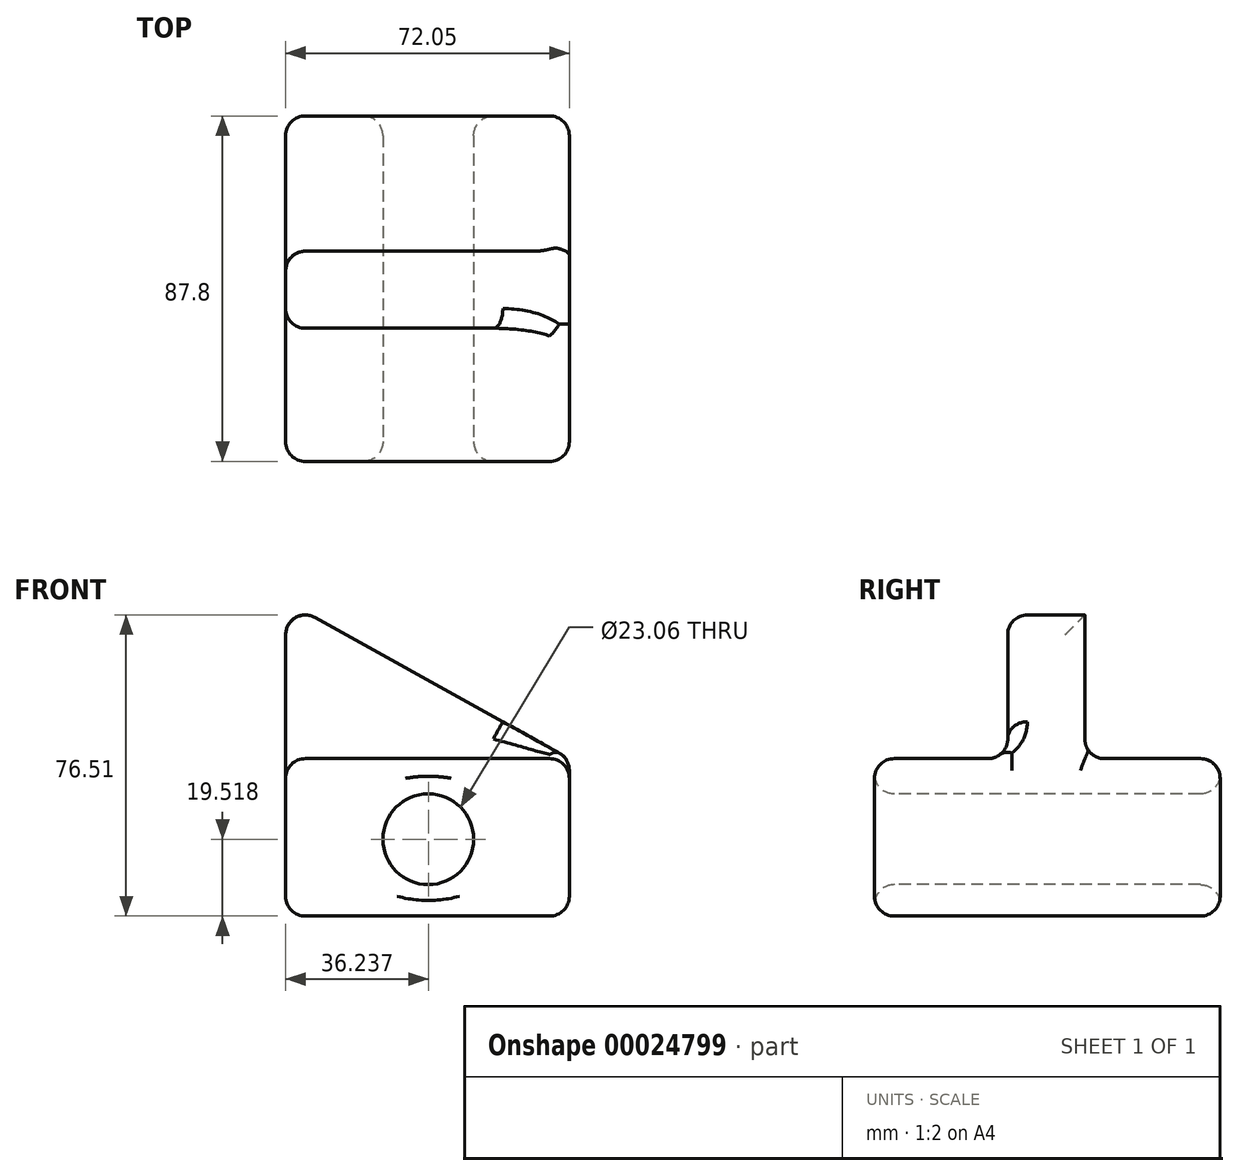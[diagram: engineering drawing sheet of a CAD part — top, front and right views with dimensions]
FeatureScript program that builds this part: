
annotation { "Feature Type Name" : "Feature", "Feature Type Description" : "" }
export const myFeature = defineFeature(function(context is Context, id is Id, definition is map)
    precondition{}
    {
        {
            var Q0;
            Q0=qCreatedBy(makeId("Top.planeOp"),FACE);
            var sketch = newSketch(context, id + "F0", { "sketchPlane" : qUnion([Q0])});
            skLineSegment(sketch, "E0.bottom", {"start": v(-59.89, -44.54) * mm, "end": v(12.16, -44.54) * mm});
            skLineSegment(sketch, "E0.top", {"start": v(-59.89, 43.26) * mm, "end": v(12.16, 43.26) * mm});
            skLineSegment(sketch, "E0.left", {"start": v(-59.89, -44.54) * mm, "end": v(-59.89, 43.26) * mm});
            skLineSegment(sketch, "E0.right", {"start": v(12.16, -44.54) * mm, "end": v(12.16, 43.26) * mm});
            skSolve(sketch);
        }
        {
            var Q0;
            Q0=makeQuery(id+"F0.imprint","IMPRINT",FACE,{"disambiguationData":[TD([[makeQuery(id+"F0.imprint","IMPRINT",EDGE,{"derivedFrom":sQuery(id+"F0.wireOp",EDGE,"E0.bottom")}),1.0]])]});
            extrude(context, id + "F1", {"entities" : qUnion([Q0]), "depth" : 40 * mm});
        }
        {
            var Q0;
            Q0=makeQuery(id+"F1.opExtrude","SWEPT_FACE",FACE,{"disambiguationData":[OSD([sQuery(id+"F0.wireOp",EDGE,"E0.bottom")])]});
            var sketch = newSketch(context, id + "F2", { "sketchPlane" : qUnion([Q0])});
            skCircle(sketch, "E1", {"center": v(-23.65, 19.52) * mm, "radius": 11.53 * mm});
            skSolve(sketch);
        }
        {
            var Q0;
            Q0=makeQuery(id+"F2.imprint","IMPRINT",FACE,{"disambiguationData":[TD([[makeQuery(id+"F2.imprint","IMPRINT",EDGE,{"derivedFrom":sQuery(id+"F2.wireOp",EDGE,"E1")}),1.0]])]});
            extrude(context, id + "F3", {"entities" : qUnion([Q0]), "operationType" : NewBodyOperationType.REMOVE, "endBound" : BoundingType.THROUGH_ALL, "oppositeDirection" : true, "depth" : 25 * mm});
        }
        {
            var Q0;
            Q0=makeQuery(id+"F1.opExtrude","CAP_FACE",FACE,{"disambiguationData":[OSD([sQuery(id+"F0.wireOp",EDGE,"E0.bottom"),sQuery(id+"F0.wireOp",EDGE,"E0.top"),sQuery(id+"F0.wireOp",EDGE,"E0.left"),sQuery(id+"F0.wireOp",EDGE,"E0.right")])],"isStart":false});
            var sketch = newSketch(context, id + "F4", { "sketchPlane" : qUnion([Q0])});
            skLineSegment(sketch, "E2.bottom", {"start": v(-59.89, -10.7) * mm, "end": v(12.16, -10.7) * mm});
            skLineSegment(sketch, "E2.top", {"start": v(-59.89, 8.88) * mm, "end": v(12.16, 8.88) * mm});
            skLineSegment(sketch, "E2.left", {"start": v(-59.89, -10.7) * mm, "end": v(-59.89, 8.88) * mm});
            skLineSegment(sketch, "E2.right", {"start": v(12.16, -10.7) * mm, "end": v(12.16, 8.88) * mm});
            skSolve(sketch);
        }
        {
            var Q0;
            Q0=makeQuery(id+"F4.imprint","IMPRINT",FACE,{"disambiguationData":[TD([[makeQuery(id+"F4.imprint","IMPRINT",EDGE,{"derivedFrom":sQuery(id+"F4.wireOp",EDGE,"E2.bottom")}),1.0]])]});
            extrude(context, id + "F5", {"entities" : qUnion([Q0]), "operationType" : NewBodyOperationType.ADD, "depth" : 40 * mm});
        }
        {
            var Q0;
            Q0=makeQuery(id+"F5.opExtrude","SWEPT_FACE",FACE,{"disambiguationData":[OSD([sQuery(id+"F4.wireOp",EDGE,"E2.bottom")])]});
            var sketch = newSketch(context, id + "F6", { "sketchPlane" : qUnion([Q0])});
            skLineSegment(sketch, "E3", {"start": v(12.16, 40) * mm, "end": v(-59.89, 80) * mm});
            skSolve(sketch);
        }
        {
            var Q0;
            Q0=makeQuery(id+"F6.imprint","IMPRINT",FACE,{"disambiguationData":[TD([[makeQuery(id+"F6.imprint","IMPRINT",EDGE,{"derivedFrom":sQuery(id+"F6.wireOp",EDGE,"E3")}),-1.0]])]});
            extrude(context, id + "F7", {"entities" : qUnion([Q0]), "operationType" : NewBodyOperationType.REMOVE, "endBound" : BoundingType.THROUGH_ALL, "oppositeDirection" : true, "depth" : 25 * mm});
        }
        {
            var Q0;
            Q0=makeQuery(id+"F5.opExtrude","SWEPT_FACE",FACE,{"disambiguationData":[OSD([sQuery(id+"F4.wireOp",EDGE,"E2.bottom")])]});
            var Q1;
            {var subQ0=sQuery(id+"F0.wireOp",EDGE,"E0.bottom");var subQ1=sQuery(id+"F0.wireOp",EDGE,"E0.left");var subQ2=sQuery(id+"F0.wireOp",EDGE,"E0.right");Q1=makeQuery(id+"F5.boolean.opBoolean","SPLIT",FACE,{"disambiguationData":[TD([makeQuery(id+"F1.opExtrude","SWEPT_FACE",FACE,{"disambiguationData":[OSD([subQ0])]})])],"derivedFrom":makeQuery(id+"F1.opExtrude","CAP_FACE",FACE,{"disambiguationData":[OSD([subQ0,sQuery(id+"F0.wireOp",EDGE,"E0.top"),subQ1,subQ2])],"isStart":false})});}
            var Q2;
            {var subQ0=sQuery(id+"F0.wireOp",EDGE,"E0.top");var subQ1=sQuery(id+"F0.wireOp",EDGE,"E0.left");var subQ2=sQuery(id+"F0.wireOp",EDGE,"E0.right");Q2=makeQuery(id+"F5.boolean.opBoolean","SPLIT",FACE,{"disambiguationData":[TD([makeQuery(id+"F1.opExtrude","SWEPT_FACE",FACE,{"disambiguationData":[OSD([subQ0])]})])],"derivedFrom":makeQuery(id+"F1.opExtrude","CAP_FACE",FACE,{"disambiguationData":[OSD([sQuery(id+"F0.wireOp",EDGE,"E0.bottom"),subQ0,subQ1,subQ2])],"isStart":false})});}
            var Q3;
            Q3=makeQuery(id+"F5.boolean.opBoolean","MERGE",FACE,{"derivedFrom":[makeQuery(id+"F1.opExtrude","SWEPT_FACE",FACE,{"disambiguationData":[OSD([sQuery(id+"F0.wireOp",EDGE,"E0.right")])]}),makeQuery(id+"F5.opExtrude","SWEPT_FACE",FACE,{"disambiguationData":[OSD([sQuery(id+"F4.wireOp",EDGE,"E2.right")])]})]});
            var Q4;
            Q4=makeQuery(id+"F1.opExtrude","SWEPT_FACE",FACE,{"disambiguationData":[OSD([sQuery(id+"F0.wireOp",EDGE,"E0.bottom")])]});
            var Q5;
            Q5=makeQuery(id+"F3.boolean.opBoolean","COPY",FACE,{"derivedFrom":makeQuery(id+"F3.opExtrude","SWEPT_FACE",FACE,{"disambiguationData":[OSD([sQuery(id+"F2.wireOp",EDGE,"E1")])]})});
            var Q6;
            Q6=makeQuery(id+"F5.boolean.opBoolean","MERGE",FACE,{"derivedFrom":[makeQuery(id+"F1.opExtrude","SWEPT_FACE",FACE,{"disambiguationData":[OSD([sQuery(id+"F0.wireOp",EDGE,"E0.left")])]}),makeQuery(id+"F5.opExtrude","SWEPT_FACE",FACE,{"disambiguationData":[OSD([sQuery(id+"F4.wireOp",EDGE,"E2.left")])]})]});
            var Q7;
            Q7=makeQuery(id+"F1.opExtrude","CAP_FACE",FACE,{"disambiguationData":[OSD([sQuery(id+"F0.wireOp",EDGE,"E0.bottom"),sQuery(id+"F0.wireOp",EDGE,"E0.top"),sQuery(id+"F0.wireOp",EDGE,"E0.left"),sQuery(id+"F0.wireOp",EDGE,"E0.right")])],"isStart":true});
            fillet(context, id + "F8", {"entities" : qUnion([Q0, Q1, Q2, Q3, Q4, Q5, Q6, Q7]), "radius" : 5 * mm, "tangentPropagation" : true, "allowEdgeOverflow" : false});
        }
    });
